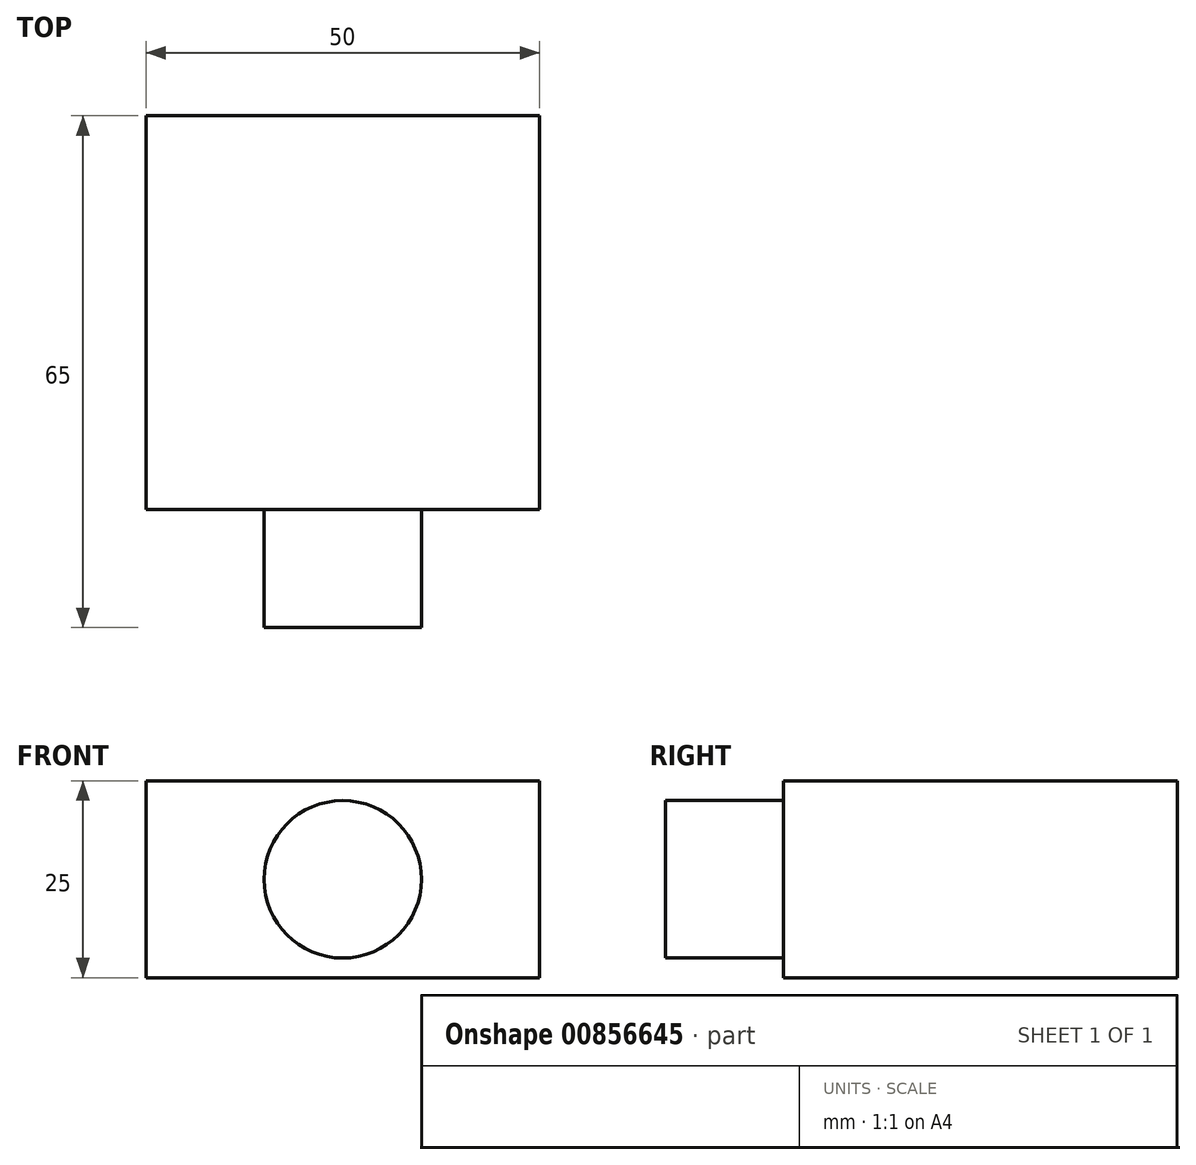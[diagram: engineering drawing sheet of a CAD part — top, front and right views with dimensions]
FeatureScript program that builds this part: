
annotation { "Feature Type Name" : "Feature", "Feature Type Description" : "" }
export const myFeature = defineFeature(function(context is Context, id is Id, definition is map)
    precondition{}
    {
        {
            var Q0;
            Q0=qCreatedBy(makeId("Top.planeOp"),FACE);
            var sketch = newSketch(context, id + "F0", { "sketchPlane" : qUnion([Q0])});
            skLineSegment(sketch, "E0.bottom", {"start": v(-25, 25) * mm, "end": v(25, 25) * mm});
            skLineSegment(sketch, "E0.top", {"start": v(-25, -25) * mm, "end": v(25, -25) * mm});
            skLineSegment(sketch, "E0.left", {"start": v(-25, 25) * mm, "end": v(-25, -25) * mm});
            skLineSegment(sketch, "E0.right", {"start": v(25, 25) * mm, "end": v(25, -25) * mm});
            skSolve(sketch);
        }
        {
            var Q0;
            Q0=makeQuery(id+"F0.imprint","IMPRINT",FACE,{"disambiguationData":[TD([[makeQuery(id+"F0.imprint","IMPRINT",EDGE,{"derivedFrom":sQuery(id+"F0.wireOp",EDGE,"E0.bottom")}),-1.0]])]});
            extrude(context, id + "F1", {"entities" : qUnion([Q0]), "depth" : 25 * mm, "offsetDistance" : 25 * mm});
        }
        {
            var Q0;
            Q0=qCreatedBy(makeId("Front.planeOp"),FACE);
            cPlane(context, id + "F2", {"entities" : qUnion([Q0]), "cplaneType" : CPlaneType.OFFSET, "offset" : 25 * mm, "width" : 150 * mm, "height" : 150 * mm});
        }
        {
            var Q0;
            Q0=qCreatedBy(id+"F2.planeOp",FACE);
            var sketch = newSketch(context, id + "F3", { "sketchPlane" : qUnion([Q0])});
            skCircle(sketch, "E1", {"center": v(0, 12.5) * mm, "radius": 10 * mm});
            skSolve(sketch);
        }
        {
            var Q0;
            Q0=makeQuery(id+"F3.imprint","IMPRINT",FACE,{"disambiguationData":[TD([[makeQuery(id+"F3.imprint","IMPRINT",EDGE,{"derivedFrom":sQuery(id+"F3.wireOp",EDGE,"E1")}),1.0]])]});
            extrude(context, id + "F4", {"entities" : qUnion([Q0]), "depth" : 15 * mm, "offsetDistance" : 25 * mm});
        }
    });
